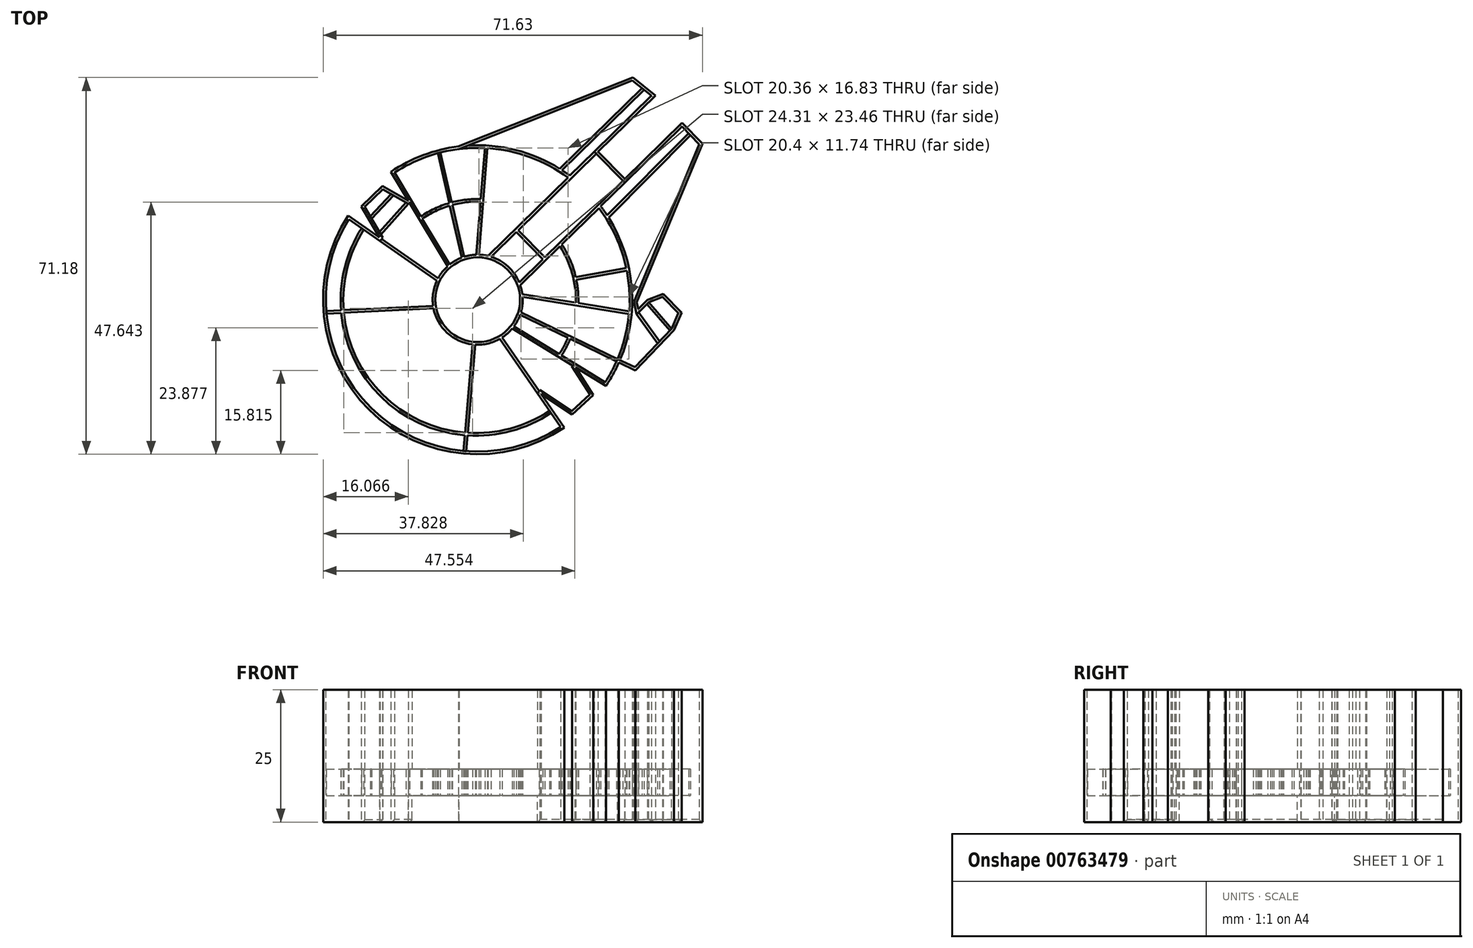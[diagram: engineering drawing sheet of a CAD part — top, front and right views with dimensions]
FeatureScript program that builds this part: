
annotation { "Feature Type Name" : "Feature", "Feature Type Description" : "" }
export const myFeature = defineFeature(function(context is Context, id is Id, definition is map)
    precondition{}
    {
        {
            var Q0;
            Q0=qCreatedBy(makeId("Top.planeOp"),FACE);
            var sketch = newSketch(context, id + "F0", { "sketchPlane" : qUnion([Q0])});
            skArc(sketch, "E0", {"start": v(9.63, 50.7) * mm, "mid": v(13.66, 13.96) * mm, "end": v(50.46, 10.62) * mm});
            skArc(sketch, "E1.0", {"start": v(9.77, 49.99) * mm, "mid": v(6.25, 41.67) * mm, "end": v(5.5, 32.67) * mm});
            skLineSegment(sketch, "E2", {"start": v(9.63, 50.7) * mm, "end": v(15.54, 46.57) * mm});
            skLineSegment(sketch, "E3", {"start": v(15.54, 46.57) * mm, "end": v(12.14, 52.43) * mm});
            skLineSegment(sketch, "E4", {"start": v(12.14, 52.43) * mm, "end": v(16.15, 56.29) * mm});
            skLineSegment(sketch, "E5", {"start": v(16.15, 56.29) * mm, "end": v(21, 53.48) * mm});
            skLineSegment(sketch, "E6", {"start": v(28.43, 41.12) * mm, "end": v(21.26, 53.06) * mm});
            skLineSegment(sketch, "E7.0", {"start": v(16.16, 46.5) * mm, "end": v(15.82, 47.1) * mm});
            skLineSegment(sketch, "E8.0", {"start": v(12.77, 52.34) * mm, "end": v(16.22, 55.67) * mm});
            skLineSegment(sketch, "E9.0", {"start": v(16.22, 55.67) * mm, "end": v(17.8, 54.75) * mm});
            skLineSegment(sketch, "E10.0", {"start": v(28.82, 41.44) * mm, "end": v(23.63, 50.08) * mm});
            skLineSegment(sketch, "E11.trimOffspring", {"start": v(9.77, 49.99) * mm, "end": v(12.18, 48.31) * mm});
            skLineSegment(sketch, "E12", {"start": v(50.46, 10.62) * mm, "end": v(46.07, 16.99) * mm});
            skLineSegment(sketch, "E13", {"start": v(46.07, 16.99) * mm, "end": v(51.9, 13.13) * mm});
            skLineSegment(sketch, "E14", {"start": v(51.9, 13.13) * mm, "end": v(55.96, 16.81) * mm});
            skLineSegment(sketch, "E15", {"start": v(55.96, 16.81) * mm, "end": v(52.61, 22.01) * mm});
            skLineSegment(sketch, "E16", {"start": v(40.62, 29.33) * mm, "end": v(52.03, 22.37) * mm});
            skLineSegment(sketch, "E17.0", {"start": v(40.93, 29.73) * mm, "end": v(49.49, 24.5) * mm});
            skLineSegment(sketch, "E18.0", {"start": v(55.31, 16.9) * mm, "end": v(51.86, 22.26) * mm});
            skLineSegment(sketch, "E19.0", {"start": v(51.86, 13.76) * mm, "end": v(55.31, 16.9) * mm});
            skLineSegment(sketch, "E20.0", {"start": v(45.82, 17.75) * mm, "end": v(51.86, 13.76) * mm});
            skLineSegment(sketch, "E21", {"start": v(45.69, 17.55) * mm, "end": v(45.82, 17.75) * mm});
            skLineSegment(sketch, "E22", {"start": v(51.86, 22.26) * mm, "end": v(52.03, 22.37) * mm});
            skLineSegment(sketch, "E23", {"start": v(16, 46.26) * mm, "end": v(16.16, 46.5) * mm});
            skLineSegment(sketch, "E24", {"start": v(21.26, 53.06) * mm, "end": v(21, 52.9) * mm});
            skLineSegment(sketch, "E25", {"start": v(30.49, 63.76) * mm, "end": v(63.42, 76.78) * mm});
            skLineSegment(sketch, "E26", {"start": v(63.42, 76.78) * mm, "end": v(67.67, 73.38) * mm});
            skLineSegment(sketch, "E27", {"start": v(67.67, 73.38) * mm, "end": v(56.84, 62.75) * mm});
            skLineSegment(sketch, "E28", {"start": v(56.84, 62.75) * mm, "end": v(61.89, 57.61) * mm});
            skLineSegment(sketch, "E29", {"start": v(72.68, 68.22) * mm, "end": v(76.55, 64.28) * mm});
            skLineSegment(sketch, "E30", {"start": v(76.55, 64.28) * mm, "end": v(64.13, 34.33) * mm});
            skLineSegment(sketch, "E31", {"start": v(64.13, 34.33) * mm, "end": v(64.43, 33.03) * mm});
            skLineSegment(sketch, "E32", {"start": v(64.43, 33.03) * mm, "end": v(66.16, 34.73) * mm});
            skLineSegment(sketch, "E33", {"start": v(66.16, 34.73) * mm, "end": v(69.15, 35.9) * mm});
            skLineSegment(sketch, "E34", {"start": v(69.15, 35.9) * mm, "end": v(72.63, 32.36) * mm});
            skLineSegment(sketch, "E35", {"start": v(72.63, 32.36) * mm, "end": v(71.16, 29.04) * mm});
            skLineSegment(sketch, "E36", {"start": v(71.16, 29.04) * mm, "end": v(63.9, 21.43) * mm});
            skLineSegment(sketch, "E37", {"start": v(63.9, 21.43) * mm, "end": v(60.78, 22.93) * mm});
            skLineSegment(sketch, "E38.0", {"start": v(32.27, 63.93) * mm, "end": v(63.33, 76.2) * mm});
            skLineSegment(sketch, "E39.0", {"start": v(63.33, 76.2) * mm, "end": v(65.12, 74.78) * mm});
            skLineSegment(sketch, "E40.0", {"start": v(66.91, 73.34) * mm, "end": v(51.52, 58.22) * mm});
            skLineSegment(sketch, "E41.0", {"start": v(56.49, 62.4) * mm, "end": v(61.53, 57.26) * mm});
            skLineSegment(sketch, "E42.0", {"start": v(42.16, 37.53) * mm, "end": v(49.64, 44.88) * mm});
            skLineSegment(sketch, "E43.0", {"start": v(72.68, 67.51) * mm, "end": v(73.94, 66.22) * mm});
            skLineSegment(sketch, "E44.0", {"start": v(75.96, 64.17) * mm, "end": v(63.61, 34.37) * mm});
            skLineSegment(sketch, "E45.0", {"start": v(63.61, 34.37) * mm, "end": v(64.13, 32.04) * mm});
            skLineSegment(sketch, "E46.0", {"start": v(64.5, 32.4) * mm, "end": v(66.08, 33.95) * mm});
            skLineSegment(sketch, "E47.0", {"start": v(66.44, 34.3) * mm, "end": v(69.03, 35.31) * mm});
            skLineSegment(sketch, "E48.0", {"start": v(69.03, 35.31) * mm, "end": v(72.03, 32.26) * mm});
            skLineSegment(sketch, "E49.0", {"start": v(72.03, 32.26) * mm, "end": v(70.73, 29.32) * mm});
            skLineSegment(sketch, "E50.0", {"start": v(70.39, 28.96) * mm, "end": v(68.44, 26.92) * mm});
            skLineSegment(sketch, "E51.0", {"start": v(63.78, 22.04) * mm, "end": v(60.98, 23.4) * mm});
            skArc(sketch, "E52.trimOffspring", {"start": v(51.52, 58.22) * mm, "mid": v(50.79, 58.75) * mm, "end": v(50.04, 59.26) * mm});
            skArc(sketch, "E53.trimOffspring", {"start": v(51.16, 57.87) * mm, "mid": v(43.96, 61.74) * mm, "end": v(35.97, 63.43) * mm});
            skArc(sketch, "E54.trimOffspring", {"start": v(58.34, 18.52) * mm, "mid": v(59.66, 20.67) * mm, "end": v(60.78, 22.93) * mm});
            skArc(sketch, "E55.trimOffspring", {"start": v(58.2, 19.2) * mm, "mid": v(59.34, 21.13) * mm, "end": v(60.33, 23.15) * mm});
            skLineSegment(sketch, "E56.trimOffspring", {"start": v(56.49, 62.4) * mm, "end": v(41.75, 47.92) * mm});
            skLineSegment(sketch, "E57.trimOffspring", {"start": v(61.89, 57.61) * mm, "end": v(72.68, 68.22) * mm});
            skLineSegment(sketch, "E58", {"start": v(73.94, 66.22) * mm, "end": v(58.57, 50.73) * mm});
            skLineSegment(sketch, "E59.0", {"start": v(74.3, 65.87) * mm, "end": v(58.84, 50.3) * mm});
            skLineSegment(sketch, "E60", {"start": v(62.27, 40.3) * mm, "end": v(52.74, 38.57) * mm});
            skLineSegment(sketch, "E61.0", {"start": v(62.17, 40.78) * mm, "end": v(52.64, 39.06) * mm});
            skLineSegment(sketch, "E62.trimOffspring", {"start": v(49.76, 10.75) * mm, "end": v(47.95, 13.39) * mm});
            skArc(sketch, "E63.trimOffspring", {"start": v(60.98, 23.4) * mm, "mid": v(63.2, 37.1) * mm, "end": v(58.84, 50.3) * mm});
            skArc(sketch, "E64.trimOffspring", {"start": v(62.17, 40.78) * mm, "mid": v(60.2, 46.73) * mm, "end": v(57, 52.11) * mm});
            skArc(sketch, "E65.trimOffspring", {"start": v(58.57, 50.73) * mm, "mid": v(57.97, 51.6) * mm, "end": v(57.35, 52.46) * mm});
            skLineSegment(sketch, "E66.trimOffspring", {"start": v(57.35, 52.46) * mm, "end": v(72.68, 67.51) * mm});
            skLineSegment(sketch, "E67.trimOffspring", {"start": v(51.16, 57.87) * mm, "end": v(36.09, 43.06) * mm});
            skLineSegment(sketch, "E68", {"start": v(50.04, 59.26) * mm, "end": v(65.51, 74.46) * mm});
            skLineSegment(sketch, "E69.0", {"start": v(49.6, 59.53) * mm, "end": v(65.12, 74.78) * mm});
            skLineSegment(sketch, "E70.trimOffspring", {"start": v(65.51, 74.46) * mm, "end": v(66.91, 73.34) * mm});
            skArc(sketch, "E71.trimOffspring", {"start": v(30.49, 63.76) * mm, "mid": v(23.82, 62.11) * mm, "end": v(17.72, 58.95) * mm});
            skLineSegment(sketch, "E72", {"start": v(35.97, 63.43) * mm, "end": v(34.33, 43.3) * mm});
            skArc(sketch, "E73", {"start": v(41.96, 38.05) * mm, "mid": v(39.84, 41.07) * mm, "end": v(36.65, 42.9) * mm});
            skCircle(sketch, "E74.0", {"center": v(34.1, 34.8) * mm, "radius": 8 * mm});
            skLineSegment(sketch, "E75.trimOffspring", {"start": v(41.96, 38.05) * mm, "end": v(46.44, 42.44) * mm});
            skArc(sketch, "E76.trimOffspring", {"start": v(36.09, 43.06) * mm, "mid": v(35.22, 43.22) * mm, "end": v(34.33, 43.3) * mm});
            skLineSegment(sketch, "E77", {"start": v(27.06, 62.6) * mm, "end": v(29.21, 53.19) * mm});
            skLineSegment(sketch, "E78", {"start": v(62.67, 32.1) * mm, "end": v(42.6, 35.35) * mm});
            skArc(sketch, "E79.trimOffspring", {"start": v(42.27, 32.43) * mm, "mid": v(42.56, 33.87) * mm, "end": v(42.6, 35.35) * mm});
            skLineSegment(sketch, "E80.trimOffspring", {"start": v(60.53, 23.6) * mm, "end": v(42.27, 32.43) * mm});
            skArc(sketch, "E81.trimOffspring", {"start": v(60.53, 23.6) * mm, "mid": v(61.93, 27.77) * mm, "end": v(62.67, 32.1) * mm});
            skLineSegment(sketch, "E82.trimOffspring", {"start": v(60.33, 23.15) * mm, "end": v(51.6, 27.37) * mm});
            skArc(sketch, "E83.trimOffspring", {"start": v(38.72, 27.66) * mm, "mid": v(39.74, 28.42) * mm, "end": v(40.62, 29.33) * mm});
            skLineSegment(sketch, "E84.trimOffspring", {"start": v(45.69, 17.55) * mm, "end": v(38.72, 27.66) * mm});
            skLineSegment(sketch, "E85.trimOffspring", {"start": v(52.61, 22.01) * mm, "end": v(58.34, 18.52) * mm});
            skArc(sketch, "E86.trimOffspring", {"start": v(40.93, 29.73) * mm, "mid": v(41.6, 30.8) * mm, "end": v(42.12, 31.95) * mm});
            skLineSegment(sketch, "E87", {"start": v(31.93, 6.19) * mm, "end": v(32.18, 9.15) * mm});
            skLineSegment(sketch, "E88", {"start": v(5.5, 32.67) * mm, "end": v(8.3, 32.8) * mm});
            skLineSegment(sketch, "E89.0", {"start": v(5.54, 32.17) * mm, "end": v(8.33, 32.3) * mm});
            skLineSegment(sketch, "E90.0", {"start": v(31.43, 6.23) * mm, "end": v(31.68, 9.19) * mm});
            skArc(sketch, "E91.trimOffspring", {"start": v(31.93, 6.19) * mm, "mid": v(41.22, 7) * mm, "end": v(49.76, 10.75) * mm});
            skArc(sketch, "E92.trimOffspring", {"start": v(5.54, 32.17) * mm, "mid": v(13.8, 14.53) * mm, "end": v(31.43, 6.23) * mm});
            skArc(sketch, "E93.trimOffspring", {"start": v(25.77, 33.14) * mm, "mid": v(28.35, 28.54) * mm, "end": v(33.14, 26.35) * mm});
            skLineSegment(sketch, "E94.trimOffspring", {"start": v(16, 46.26) * mm, "end": v(26.63, 38.84) * mm});
            skArc(sketch, "E95.trimOffspring", {"start": v(26.4, 38.39) * mm, "mid": v(25.7, 36.07) * mm, "end": v(25.69, 33.64) * mm});
            skArc(sketch, "E96.trimOffspring", {"start": v(33.64, 26.3) * mm, "mid": v(36.05, 26.52) * mm, "end": v(38.3, 27.4) * mm});
            skArc(sketch, "E97.trimOffspring", {"start": v(28.43, 41.12) * mm, "mid": v(27.43, 40.06) * mm, "end": v(26.63, 38.84) * mm});
            skLineSegment(sketch, "E98", {"start": v(46.8, 42.8) * mm, "end": v(41.75, 47.92) * mm});
            skLineSegment(sketch, "E99.0", {"start": v(46.44, 42.44) * mm, "end": v(41.4, 47.57) * mm});
            skLineSegment(sketch, "E100.trimOffspring", {"start": v(46.8, 42.8) * mm, "end": v(61.53, 57.26) * mm});
            skLineSegment(sketch, "E101.trimOffspring", {"start": v(41.4, 47.57) * mm, "end": v(36.64, 42.9) * mm});
            skArc(sketch, "E102.trimOffspring", {"start": v(49.91, 24.25) * mm, "mid": v(50.83, 25.77) * mm, "end": v(51.6, 27.37) * mm});
            skArc(sketch, "E103.trimOffspring", {"start": v(53.1, 34.15) * mm, "mid": v(53.06, 36.37) * mm, "end": v(52.74, 38.57) * mm});
            skArc(sketch, "E104.trimOffspring", {"start": v(34.69, 53.82) * mm, "mid": v(31.93, 53.7) * mm, "end": v(29.21, 53.19) * mm});
            skLineSegment(sketch, "E105.0", {"start": v(62.72, 32.6) * mm, "end": v(53.1, 34.15) * mm});
            skArc(sketch, "E106.0", {"start": v(52.61, 34.23) * mm, "mid": v(51.94, 39.79) * mm, "end": v(49.64, 44.88) * mm});
            skLineSegment(sketch, "E107.0", {"start": v(26.58, 62.48) * mm, "end": v(28.73, 53.05) * mm});
            skLineSegment(sketch, "E108.0", {"start": v(35.47, 63.45) * mm, "end": v(34.69, 53.82) * mm});
            skArc(sketch, "E109.0", {"start": v(49.49, 24.5) * mm, "mid": v(50.4, 26) * mm, "end": v(51.15, 27.59) * mm});
            skLineSegment(sketch, "E110.trimOffspring", {"start": v(49.91, 24.25) * mm, "end": v(58.2, 19.2) * mm});
            skLineSegment(sketch, "E111.trimOffspring", {"start": v(51.15, 27.59) * mm, "end": v(42.12, 31.95) * mm});
            skLineSegment(sketch, "E112.trimOffspring", {"start": v(52.61, 34.23) * mm, "end": v(42.54, 35.86) * mm});
            skArc(sketch, "E113.trimOffspring", {"start": v(52.64, 39.06) * mm, "mid": v(51.6, 42.27) * mm, "end": v(50, 45.24) * mm});
            skLineSegment(sketch, "E114.trimOffspring", {"start": v(50, 45.24) * mm, "end": v(57, 52.11) * mm});
            skArc(sketch, "E115.trimOffspring", {"start": v(33.83, 43.29) * mm, "mid": v(32.68, 43.17) * mm, "end": v(31.56, 42.9) * mm});
            skArc(sketch, "E116.trimOffspring", {"start": v(31.08, 42.74) * mm, "mid": v(29.9, 42.18) * mm, "end": v(28.82, 41.44) * mm});
            skArc(sketch, "E117.trimOffspring", {"start": v(28.84, 52.56) * mm, "mid": v(26.14, 51.52) * mm, "end": v(23.63, 50.08) * mm});
            skLineSegment(sketch, "E118.trimOffspring", {"start": v(29.32, 52.7) * mm, "end": v(31.56, 42.9) * mm});
            skArc(sketch, "E119.trimOffspring", {"start": v(28.73, 53.05) * mm, "mid": v(25.95, 51.99) * mm, "end": v(23.37, 50.5) * mm});
            skLineSegment(sketch, "E120.trimOffspring", {"start": v(28.84, 52.56) * mm, "end": v(31.08, 42.74) * mm});
            skLineSegment(sketch, "E121.trimOffspring", {"start": v(34.65, 53.32) * mm, "end": v(33.83, 43.29) * mm});
            skArc(sketch, "E122.trimOffspring", {"start": v(34.65, 53.32) * mm, "mid": v(31.96, 53.2) * mm, "end": v(29.32, 52.7) * mm});
            skArc(sketch, "E123.trimOffspring", {"start": v(42.54, 35.86) * mm, "mid": v(42.4, 36.7) * mm, "end": v(42.16, 37.53) * mm});
            skArc(sketch, "E124.trimOffspring", {"start": v(35.47, 63.45) * mm, "mid": v(31.23, 63.34) * mm, "end": v(27.06, 62.6) * mm});
            skArc(sketch, "E125.trimOffspring", {"start": v(26.58, 62.48) * mm, "mid": v(22.34, 60.96) * mm, "end": v(18.4, 58.8) * mm});
            skArc(sketch, "E126", {"start": v(12.59, 48.02) * mm, "mid": v(9.47, 40.73) * mm, "end": v(8.79, 32.83) * mm});
            skPoint(sketch, "E126.endSnap0", {"position": v(48.27, 13.8) * mm});
            skArc(sketch, "E127.0", {"start": v(12.18, 48.31) * mm, "mid": v(8.99, 40.87) * mm, "end": v(8.3, 32.8) * mm});
            skArc(sketch, "E128.trimOffspring", {"start": v(32.22, 9.65) * mm, "mid": v(40.28, 10.46) * mm, "end": v(47.66, 13.8) * mm});
            skLineSegment(sketch, "E129.trimOffspring", {"start": v(32.22, 9.65) * mm, "end": v(33.64, 26.3) * mm});
            skArc(sketch, "E130.trimOffspring", {"start": v(32.18, 9.15) * mm, "mid": v(40.41, 9.98) * mm, "end": v(47.95, 13.39) * mm});
            skLineSegment(sketch, "E131.trimOffspring", {"start": v(31.73, 9.69) * mm, "end": v(33.14, 26.35) * mm});
            skLineSegment(sketch, "E132.trimOffspring", {"start": v(8.79, 32.83) * mm, "end": v(25.69, 33.64) * mm});
            skLineSegment(sketch, "E133.trimOffspring", {"start": v(8.83, 32.33) * mm, "end": v(25.77, 33.14) * mm});
            skArc(sketch, "E134.trimOffspring", {"start": v(8.33, 32.3) * mm, "mid": v(15.8, 16.5) * mm, "end": v(31.68, 9.19) * mm});
            skArc(sketch, "E135.trimOffspring", {"start": v(8.83, 32.33) * mm, "mid": v(16.16, 16.84) * mm, "end": v(31.73, 9.69) * mm});
            skLineSegment(sketch, "E136.trimOffspring", {"start": v(12.59, 48.02) * mm, "end": v(26.4, 38.39) * mm});
            skLineSegment(sketch, "E137.trimOffspring", {"start": v(21, 53.48) * mm, "end": v(17.72, 58.95) * mm});
            skLineSegment(sketch, "E138", {"start": v(66.44, 34.3) * mm, "end": v(70.73, 29.32) * mm});
            skLineSegment(sketch, "E139", {"start": v(64.13, 32.04) * mm, "end": v(68.09, 26.55) * mm});
            skLineSegment(sketch, "E140.0", {"start": v(64.5, 32.4) * mm, "end": v(68.44, 26.92) * mm});
            skLineSegment(sketch, "E141.0", {"start": v(66.08, 33.95) * mm, "end": v(70.39, 28.96) * mm});
            skLineSegment(sketch, "E142.trimOffspring", {"start": v(68.09, 26.55) * mm, "end": v(63.78, 22.04) * mm});
            skLineSegment(sketch, "E143", {"start": v(15.82, 47.1) * mm, "end": v(21, 52.9) * mm});
            skLineSegment(sketch, "E144", {"start": v(14.07, 50.1) * mm, "end": v(18.25, 54.5) * mm});
            skLineSegment(sketch, "E145.0", {"start": v(13.8, 50.56) * mm, "end": v(17.8, 54.75) * mm});
            skLineSegment(sketch, "E146.0", {"start": v(15.55, 47.55) * mm, "end": v(20.56, 53.16) * mm});
            skLineSegment(sketch, "E147.trimOffspring", {"start": v(15.55, 47.55) * mm, "end": v(14.07, 50.1) * mm});
            skLineSegment(sketch, "E148.trimOffspring", {"start": v(13.8, 50.56) * mm, "end": v(12.77, 52.34) * mm});
            skLineSegment(sketch, "E149.trimOffspring", {"start": v(18.25, 54.5) * mm, "end": v(20.56, 53.16) * mm});
            skLineSegment(sketch, "E150.trimOffspring", {"start": v(47.66, 13.8) * mm, "end": v(38.3, 27.4) * mm});
            skLineSegment(sketch, "E151.trimOffspring", {"start": v(74.3, 65.87) * mm, "end": v(75.96, 64.17) * mm});
            skArc(sketch, "E152.trimOffspring", {"start": v(49.6, 59.53) * mm, "mid": v(41.28, 63.1) * mm, "end": v(32.27, 63.93) * mm});
            skArc(sketch, "E153.trimOffspring", {"start": v(62.72, 32.6) * mm, "mid": v(62.75, 36.46) * mm, "end": v(62.27, 40.3) * mm});
            skLineSegment(sketch, "E154.trimOffspring", {"start": v(23.37, 50.5) * mm, "end": v(18.4, 58.8) * mm});
            skSolve(sketch);
        }
        {
            var Q0;
            Q0=makeQuery(id+"F0.imprint","IMPRINT",FACE,{"disambiguationData":[TD([[makeQuery(id+"F0.imprint","IMPRINT",EDGE,{"derivedFrom":sQuery(id+"F0.wireOp",EDGE,"3ed46772-27a6-4d94-b4a7-c1b057d9c120.2.1")}),1.0]])]});
            var Q1;
            Q1=makeQuery(id+"F0.imprint","IMPRINT",FACE,{"disambiguationData":[TD([[makeQuery(id+"F0.imprint","IMPRINT",EDGE,{"derivedFrom":sQuery(id+"F0.wireOp",EDGE,"3ed46772-27a6-4d94-b4a7-c1b057d9c120.1.1")}),1.0]])]});
            var Q2;
            Q2=makeQuery(id+"F0.imprint","IMPRINT",FACE,{"disambiguationData":[TD([[makeQuery(id+"F0.imprint","IMPRINT",EDGE,{"derivedFrom":sQuery(id+"F0.wireOp",EDGE,"3iVvSaAU-kiet-Srhm-uzs1-kmzdiTIg7kjV")}),-1.0]])]});
            var Q3;
            Q3=makeQuery(id+"F0.imprint","IMPRINT",FACE,{"disambiguationData":[TD([[makeQuery(id+"F0.imprint","IMPRINT",EDGE,{"derivedFrom":sQuery(id+"F0.wireOp",EDGE,"gFyHxgtJ-ju8G-WbUf-OddL-X56tFMkTOzbv")}),1.0]])]});
            var Q4;
            Q4=makeQuery(id+"F0.imprint","IMPRINT",FACE,{"disambiguationData":[TD([[makeQuery(id+"F0.imprint","IMPRINT",EDGE,{"derivedFrom":sQuery(id+"F0.wireOp",EDGE,"a3401636-6155-42f7-9479-38b70ebc3d2b.1.0")}),1.0]])]});
            var Q5;
            Q5=makeQuery(id+"F0.imprint","IMPRINT",FACE,{"disambiguationData":[TD([[makeQuery(id+"F0.imprint","IMPRINT",EDGE,{"derivedFrom":sQuery(id+"F0.wireOp",EDGE,"a3401636-6155-42f7-9479-38b70ebc3d2b.2.0")}),1.0]])]});
            var Q6;
            Q6=makeQuery(id+"F0.imprint","IMPRINT",FACE,{"disambiguationData":[TD([[makeQuery(id+"F0.imprint","IMPRINT",EDGE,{"derivedFrom":sQuery(id+"F0.wireOp",EDGE,"e8Qt5wkm-OQUc-Hg0l-7nr0-fbRjWDWY3zNd")}),-1.0]])]});
            var Q7;
            Q7=makeQuery(id+"F0.imprint","IMPRINT",FACE,{"disambiguationData":[TD([[makeQuery(id+"F0.imprint","IMPRINT",EDGE,{"derivedFrom":sQuery(id+"F0.wireOp",EDGE,"2Ig4vxbF-eVPD-97Q4-TkuO-rgopO8nLGlP4")}),-1.0]])]});
            var Q8;
            Q8=makeQuery(id+"F0.imprint","IMPRINT",FACE,{"disambiguationData":[TD([[makeQuery(id+"F0.imprint","IMPRINT",EDGE,{"derivedFrom":sQuery(id+"F0.wireOp",EDGE,"u05zh7sX-OJC8-3TQU-wVel-wsQ1eLN49gEu")}),1.0]])]});
            var Q9;
            Q9=makeQuery(id+"F0.imprint","IMPRINT",FACE,{"disambiguationData":[TD([[makeQuery(id+"F0.imprint","IMPRINT",EDGE,{"derivedFrom":sQuery(id+"F0.wireOp",EDGE,"xzO9axfg-FktW-NyAH-tsz7-sGytwWePR5oS")}),1.0]])]});
            var Q10;
            Q10=makeQuery(id+"F0.imprint","IMPRINT",FACE,{"disambiguationData":[TD([[makeQuery(id+"F0.imprint","IMPRINT",EDGE,{"derivedFrom":sQuery(id+"F0.wireOp",EDGE,"E0")}),1.0]])]});
            extrude(context, id + "F1", {"entities" : qUnion([Q0, Q1, Q2, Q3, Q4, Q5, Q6, Q7, Q8, Q9, Q10]), "depth" : 25 * mm, "offsetDistance" : 25 * mm});
        }
        {
            var Q0;
            Q0=qCreatedBy(makeId("Top.planeOp"),FACE);
            cPlane(context, id + "F2", {"entities" : qUnion([Q0]), "cplaneType" : CPlaneType.OFFSET, "offset" : 5 * mm, "width" : 150 * mm, "height" : 150 * mm});
        }
        {
            var Q0;
            Q0=qCreatedBy(id+"F2.planeOp",FACE);
            var sketch = newSketch(context, id + "F3", { "sketchPlane" : qUnion([Q0])});
            skArc(sketch, "E155.0", {"start": v(9.77, 49.99) * mm, "mid": v(6.25, 41.67) * mm, "end": v(5.5, 32.67) * mm});
            skLineSegment(sketch, "E156.0", {"start": v(16.16, 46.5) * mm, "end": v(15.55, 47.55) * mm});
            skLineSegment(sketch, "E157.0", {"start": v(12.77, 52.34) * mm, "end": v(16.22, 55.67) * mm});
            skLineSegment(sketch, "E158.0", {"start": v(16.22, 55.67) * mm, "end": v(18.25, 54.5) * mm});
            skLineSegment(sketch, "E159.trimOffspring", {"start": v(9.77, 49.99) * mm, "end": v(15.7, 45.85) * mm});
            skLineSegment(sketch, "E160.0", {"start": v(55.31, 16.9) * mm, "end": v(51.86, 22.26) * mm});
            skLineSegment(sketch, "E161.0", {"start": v(51.86, 13.76) * mm, "end": v(55.31, 16.9) * mm});
            skLineSegment(sketch, "E162.0", {"start": v(45.82, 17.75) * mm, "end": v(51.86, 13.76) * mm});
            skLineSegment(sketch, "E163", {"start": v(45.39, 17.1) * mm, "end": v(45.82, 17.75) * mm});
            skLineSegment(sketch, "E164", {"start": v(51.86, 22.26) * mm, "end": v(52.5, 22.67) * mm});
            skLineSegment(sketch, "E165", {"start": v(15.7, 45.85) * mm, "end": v(16.16, 46.5) * mm});
            skLineSegment(sketch, "E166", {"start": v(21.69, 53.31) * mm, "end": v(21, 52.9) * mm});
            skLineSegment(sketch, "E167.0", {"start": v(30.61, 63.27) * mm, "end": v(63.33, 76.2) * mm});
            skLineSegment(sketch, "E168.0", {"start": v(63.33, 76.2) * mm, "end": v(66.91, 73.34) * mm});
            skLineSegment(sketch, "E169.0", {"start": v(66.91, 73.34) * mm, "end": v(56.14, 62.75) * mm});
            skLineSegment(sketch, "E170.0", {"start": v(56.14, 62.75) * mm, "end": v(61.88, 56.9) * mm});
            skLineSegment(sketch, "E171.0", {"start": v(72.68, 67.51) * mm, "end": v(75.96, 64.17) * mm});
            skLineSegment(sketch, "E172.0", {"start": v(75.96, 64.17) * mm, "end": v(63.61, 34.37) * mm});
            skLineSegment(sketch, "E173.0", {"start": v(63.61, 34.37) * mm, "end": v(64.13, 32.04) * mm});
            skLineSegment(sketch, "E174.0", {"start": v(64.13, 32.04) * mm, "end": v(66.44, 34.3) * mm});
            skLineSegment(sketch, "E175.0", {"start": v(66.44, 34.3) * mm, "end": v(69.03, 35.31) * mm});
            skLineSegment(sketch, "E176.0", {"start": v(69.03, 35.31) * mm, "end": v(72.03, 32.26) * mm});
            skLineSegment(sketch, "E177.0", {"start": v(72.03, 32.26) * mm, "end": v(70.73, 29.32) * mm});
            skLineSegment(sketch, "E178.0", {"start": v(70.73, 29.32) * mm, "end": v(68.09, 26.55) * mm});
            skLineSegment(sketch, "E179.0", {"start": v(63.78, 22.04) * mm, "end": v(60.53, 23.6) * mm});
            skArc(sketch, "E180.trimOffspring", {"start": v(58.2, 19.2) * mm, "mid": v(59.46, 21.35) * mm, "end": v(60.53, 23.6) * mm});
            skLineSegment(sketch, "E181.0", {"start": v(74.3, 65.87) * mm, "end": v(74.3, 65.87) * mm});
            skLineSegment(sketch, "E182.trimOffspring", {"start": v(49.76, 10.75) * mm, "end": v(47.95, 13.39) * mm});
            skLineSegment(sketch, "E183.trimOffspring", {"start": v(61.88, 56.9) * mm, "end": v(72.68, 67.51) * mm});
            skArc(sketch, "E184.trimOffspring", {"start": v(31.43, 6.23) * mm, "mid": v(40.98, 6.94) * mm, "end": v(49.76, 10.75) * mm});
            skArc(sketch, "E185.trimOffspring", {"start": v(5.5, 32.67) * mm, "mid": v(13.63, 14.7) * mm, "end": v(31.43, 6.23) * mm});
            skLineSegment(sketch, "E186.trimOffspring", {"start": v(52.5, 22.67) * mm, "end": v(58.2, 19.2) * mm});
            skArc(sketch, "E187.trimOffspring", {"start": v(30.61, 63.27) * mm, "mid": v(28.83, 63) * mm, "end": v(27.06, 62.6) * mm});
            skArc(sketch, "E188.trimOffspring", {"start": v(27.06, 62.6) * mm, "mid": v(22.57, 61.06) * mm, "end": v(18.4, 58.8) * mm});
            skPoint(sketch, "E189.endSnap0", {"position": v(48.27, 13.8) * mm});
            skLineSegment(sketch, "E190.trimOffspring", {"start": v(68.09, 26.55) * mm, "end": v(63.78, 22.04) * mm});
            skLineSegment(sketch, "E191.trimOffspring", {"start": v(15.55, 47.55) * mm, "end": v(13.8, 50.56) * mm});
            skLineSegment(sketch, "E192.trimOffspring", {"start": v(13.8, 50.56) * mm, "end": v(12.77, 52.34) * mm});
            skLineSegment(sketch, "E193.trimOffspring", {"start": v(18.25, 54.5) * mm, "end": v(21, 52.9) * mm});
            skLineSegment(sketch, "E194.trimOffspring", {"start": v(47.95, 13.39) * mm, "end": v(45.39, 17.1) * mm});
            skLineSegment(sketch, "E195.trimOffspring", {"start": v(21.69, 53.31) * mm, "end": v(18.4, 58.8) * mm});
            skPoint(sketch, "E196.trimOffspring.end.orphan", {"position": v(47.66, 13.8) * mm});
            skSolve(sketch);
        }
        {
            var Q0;
            Q0 = qSketchRegion(id + "F3", true);
            extrude(context, id + "F4", {"entities" : qUnion([Q0]), "operationType" : NewBodyOperationType.REMOVE, "oppositeDirection" : true, "depth" : 5 * mm, "offsetDistance" : 25 * mm});
        }
        {
            var Q0;
            Q0=qCreatedBy(id+"F2.planeOp",FACE);
            cPlane(context, id + "F5", {"entities" : qUnion([Q0]), "cplaneType" : CPlaneType.OFFSET, "offset" : 5 * mm, "width" : 150 * mm, "height" : 150 * mm});
        }
        {
            var Q0;
            Q0=qCreatedBy(id+"F5.planeOp",FACE);
            var sketch = newSketch(context, id + "F6", { "sketchPlane" : qUnion([Q0])});
            skArc(sketch, "E197.0", {"start": v(9.77, 49.99) * mm, "mid": v(6.25, 41.67) * mm, "end": v(5.5, 32.67) * mm});
            skLineSegment(sketch, "E198.0", {"start": v(16.16, 46.5) * mm, "end": v(15.55, 47.55) * mm});
            skLineSegment(sketch, "E199.0", {"start": v(12.77, 52.34) * mm, "end": v(16.22, 55.67) * mm});
            skLineSegment(sketch, "E200.0", {"start": v(16.22, 55.67) * mm, "end": v(18.25, 54.5) * mm});
            skLineSegment(sketch, "E201.trimOffspring", {"start": v(9.77, 49.99) * mm, "end": v(15.7, 45.85) * mm});
            skLineSegment(sketch, "E202.0", {"start": v(55.31, 16.9) * mm, "end": v(51.86, 22.26) * mm});
            skLineSegment(sketch, "E203.0", {"start": v(51.86, 13.76) * mm, "end": v(55.31, 16.9) * mm});
            skLineSegment(sketch, "E204.0", {"start": v(45.82, 17.75) * mm, "end": v(51.86, 13.76) * mm});
            skLineSegment(sketch, "E205", {"start": v(45.39, 17.1) * mm, "end": v(45.82, 17.75) * mm});
            skLineSegment(sketch, "E206", {"start": v(51.86, 22.26) * mm, "end": v(52.5, 22.67) * mm});
            skLineSegment(sketch, "E207", {"start": v(15.7, 45.85) * mm, "end": v(16.16, 46.5) * mm});
            skLineSegment(sketch, "E208", {"start": v(21.69, 53.31) * mm, "end": v(21, 52.9) * mm});
            skLineSegment(sketch, "E209.0", {"start": v(30.61, 63.27) * mm, "end": v(63.33, 76.2) * mm});
            skLineSegment(sketch, "E210.0", {"start": v(63.33, 76.2) * mm, "end": v(66.91, 73.34) * mm});
            skLineSegment(sketch, "E211.0", {"start": v(66.91, 73.34) * mm, "end": v(56.14, 62.75) * mm});
            skLineSegment(sketch, "E212.0", {"start": v(56.14, 62.75) * mm, "end": v(61.88, 56.9) * mm});
            skLineSegment(sketch, "E213.0", {"start": v(72.68, 67.51) * mm, "end": v(75.96, 64.17) * mm});
            skLineSegment(sketch, "E214.0", {"start": v(75.96, 64.17) * mm, "end": v(63.61, 34.37) * mm});
            skLineSegment(sketch, "E215.0", {"start": v(63.61, 34.37) * mm, "end": v(64.13, 32.04) * mm});
            skLineSegment(sketch, "E216.0", {"start": v(64.13, 32.04) * mm, "end": v(66.44, 34.3) * mm});
            skLineSegment(sketch, "E217.0", {"start": v(66.44, 34.3) * mm, "end": v(69.03, 35.31) * mm});
            skLineSegment(sketch, "E218.0", {"start": v(69.03, 35.31) * mm, "end": v(72.03, 32.26) * mm});
            skLineSegment(sketch, "E219.0", {"start": v(72.03, 32.26) * mm, "end": v(70.73, 29.32) * mm});
            skLineSegment(sketch, "E220.0", {"start": v(70.73, 29.32) * mm, "end": v(68.09, 26.55) * mm});
            skLineSegment(sketch, "E221.0", {"start": v(63.78, 22.04) * mm, "end": v(60.53, 23.6) * mm});
            skArc(sketch, "E222.trimOffspring", {"start": v(58.2, 19.2) * mm, "mid": v(59.46, 21.35) * mm, "end": v(60.53, 23.6) * mm});
            skLineSegment(sketch, "E223.0", {"start": v(74.3, 65.87) * mm, "end": v(74.3, 65.87) * mm});
            skLineSegment(sketch, "E224.trimOffspring", {"start": v(49.76, 10.75) * mm, "end": v(47.95, 13.39) * mm});
            skLineSegment(sketch, "E225.trimOffspring", {"start": v(61.88, 56.9) * mm, "end": v(72.68, 67.51) * mm});
            skArc(sketch, "E226.trimOffspring", {"start": v(31.43, 6.23) * mm, "mid": v(40.98, 6.94) * mm, "end": v(49.76, 10.75) * mm});
            skArc(sketch, "E227.trimOffspring", {"start": v(5.5, 32.67) * mm, "mid": v(13.63, 14.7) * mm, "end": v(31.43, 6.23) * mm});
            skLineSegment(sketch, "E228.trimOffspring", {"start": v(52.5, 22.67) * mm, "end": v(58.2, 19.2) * mm});
            skArc(sketch, "E229.trimOffspring", {"start": v(30.61, 63.27) * mm, "mid": v(28.83, 63) * mm, "end": v(27.06, 62.6) * mm});
            skArc(sketch, "E230.trimOffspring", {"start": v(27.06, 62.6) * mm, "mid": v(22.57, 61.06) * mm, "end": v(18.4, 58.8) * mm});
            skPoint(sketch, "E231.endSnap0", {"position": v(48.27, 13.8) * mm});
            skLineSegment(sketch, "E232.trimOffspring", {"start": v(68.09, 26.55) * mm, "end": v(63.78, 22.04) * mm});
            skLineSegment(sketch, "E233.trimOffspring", {"start": v(15.55, 47.55) * mm, "end": v(13.8, 50.56) * mm});
            skLineSegment(sketch, "E234.trimOffspring", {"start": v(13.8, 50.56) * mm, "end": v(12.77, 52.34) * mm});
            skLineSegment(sketch, "E235.trimOffspring", {"start": v(18.25, 54.5) * mm, "end": v(21, 52.9) * mm});
            skLineSegment(sketch, "E236.trimOffspring", {"start": v(47.95, 13.39) * mm, "end": v(45.39, 17.1) * mm});
            skLineSegment(sketch, "E237.trimOffspring", {"start": v(21.69, 53.31) * mm, "end": v(18.4, 58.8) * mm});
            skPoint(sketch, "E238.trimOffspring.end.orphan", {"position": v(47.66, 13.8) * mm});
            skSolve(sketch);
        }
        {
            var Q0;
            Q0 = qSketchRegion(id + "F6", true);
            extrude(context, id + "F7", {"entities" : qUnion([Q0]), "operationType" : NewBodyOperationType.REMOVE, "depth" : 15 * mm, "offsetDistance" : 25 * mm});
        }
        {
            var Q0;
            Q0=makeQuery(id+"F1.opExtrude","CAP_EDGE",EDGE,{"disambiguationData":[OSD([sQuery(id+"F0.wireOp",EDGE,"E44.0")])],"isStart":true});
            var Q1;
            Q1=makeQuery(id+"F4.boolean.opBoolean","MERGE",EDGE,{"derivedFrom":[makeQuery(id+"F1.opExtrude","CAP_EDGE",EDGE,{"disambiguationData":[OSD([sQuery(id+"F0.wireOp",EDGE,"E43.0")])],"isStart":true}),makeQuery(id+"F1.opExtrude","CAP_EDGE",EDGE,{"disambiguationData":[OSD([sQuery(id+"F0.wireOp",EDGE,"E151.trimOffspring")])],"isStart":true}),makeQuery(id+"F4.opExtrude","CAP_EDGE",EDGE,{"disambiguationData":[OSD([sQuery(id+"F3.wireOp",EDGE,"E171.0")])],"isStart":false})]});
            var Q2;
            Q2=makeQuery(id+"F1.opExtrude","CAP_EDGE",EDGE,{"disambiguationData":[OSD([sQuery(id+"F0.wireOp",EDGE,"E66.trimOffspring")])],"isStart":true});
            var Q3;
            Q3=makeQuery(id+"F4.boolean.opBoolean","MERGE",EDGE,{"derivedFrom":[makeQuery(id+"F1.opExtrude","CAP_EDGE",EDGE,{"disambiguationData":[OSD([sQuery(id+"F0.wireOp",EDGE,"E41.0")])],"isStart":true}),makeQuery(id+"F4.opExtrude","CAP_EDGE",EDGE,{"disambiguationData":[OSD([sQuery(id+"F3.wireOp",EDGE,"E170.0")])],"isStart":false})]});
            var Q4;
            Q4=makeQuery(id+"F1.opExtrude","CAP_EDGE",EDGE,{"disambiguationData":[OSD([sQuery(id+"F0.wireOp",EDGE,"E40.0")])],"isStart":true});
            var Q5;
            Q5=makeQuery(id+"F4.boolean.opBoolean","MERGE",EDGE,{"derivedFrom":[makeQuery(id+"F1.opExtrude","CAP_EDGE",EDGE,{"disambiguationData":[OSD([sQuery(id+"F0.wireOp",EDGE,"E39.0")])],"isStart":true}),makeQuery(id+"F1.opExtrude","CAP_EDGE",EDGE,{"disambiguationData":[OSD([sQuery(id+"F0.wireOp",EDGE,"E70.trimOffspring")])],"isStart":true}),makeQuery(id+"F4.opExtrude","CAP_EDGE",EDGE,{"disambiguationData":[OSD([sQuery(id+"F3.wireOp",EDGE,"E168.0")])],"isStart":false})]});
            var Q6;
            Q6=makeQuery(id+"F4.boolean.opBoolean","MERGE",EDGE,{"derivedFrom":[makeQuery(id+"F1.opExtrude","CAP_EDGE",EDGE,{"disambiguationData":[OSD([sQuery(id+"F0.wireOp",EDGE,"E38.0")])],"isStart":true}),makeQuery(id+"F4.opExtrude","CAP_EDGE",EDGE,{"disambiguationData":[OSD([sQuery(id+"F3.wireOp",EDGE,"E167.0")])],"isStart":false})]});
            var Q7;
            Q7=makeQuery(id+"F4.boolean.opBoolean","MERGE",EDGE,{"derivedFrom":[makeQuery(id+"F1.opExtrude","CAP_EDGE",EDGE,{"disambiguationData":[OSD([sQuery(id+"F0.wireOp",EDGE,"E124.trimOffspring")])],"isStart":true}),makeQuery(id+"F1.opExtrude","CAP_EDGE",EDGE,{"disambiguationData":[OSD([sQuery(id+"F0.wireOp",EDGE,"E125.trimOffspring")])],"isStart":true}),makeQuery(id+"F4.opExtrude","CAP_EDGE",EDGE,{"disambiguationData":[OSD([sQuery(id+"F3.wireOp",EDGE,"E187.trimOffspring"),sQuery(id+"F3.wireOp",EDGE,"E188.trimOffspring")])],"isStart":false})]});
            var Q8;
            Q8=makeQuery(id+"F1.opExtrude","CAP_EDGE",EDGE,{"disambiguationData":[OSD([sQuery(id+"F0.wireOp",EDGE,"E154.trimOffspring")])],"isStart":true});
            var Q9;
            Q9=makeQuery(id+"F4.boolean.opBoolean","MERGE",EDGE,{"derivedFrom":[makeQuery(id+"F1.opExtrude","CAP_EDGE",EDGE,{"disambiguationData":[OSD([sQuery(id+"F0.wireOp",EDGE,"E24")])],"isStart":true}),makeQuery(id+"F4.opExtrude","CAP_EDGE",EDGE,{"disambiguationData":[OSD([sQuery(id+"F3.wireOp",EDGE,"E166")])],"isStart":false})]});
            var Q10;
            Q10=makeQuery(id+"F4.boolean.opBoolean","MERGE",EDGE,{"derivedFrom":[makeQuery(id+"F1.opExtrude","CAP_EDGE",EDGE,{"disambiguationData":[OSD([sQuery(id+"F0.wireOp",EDGE,"E9.0")])],"isStart":true}),makeQuery(id+"F1.opExtrude","CAP_EDGE",EDGE,{"disambiguationData":[OSD([sQuery(id+"F0.wireOp",EDGE,"E149.trimOffspring")])],"isStart":true}),makeQuery(id+"F4.opExtrude","CAP_EDGE",EDGE,{"disambiguationData":[OSD([sQuery(id+"F3.wireOp",EDGE,"E158.0"),sQuery(id+"F3.wireOp",EDGE,"E193.trimOffspring")])],"isStart":false})]});
            var Q11;
            Q11=makeQuery(id+"F1.opExtrude","CAP_EDGE",EDGE,{"disambiguationData":[OSD([sQuery(id+"F0.wireOp",EDGE,"E8.0")])],"isStart":true});
            var Q12;
            Q12=makeQuery(id+"F4.boolean.opBoolean","MERGE",EDGE,{"derivedFrom":[makeQuery(id+"F1.opExtrude","CAP_EDGE",EDGE,{"disambiguationData":[OSD([sQuery(id+"F0.wireOp",EDGE,"E7.0")])],"isStart":true}),makeQuery(id+"F1.opExtrude","CAP_EDGE",EDGE,{"disambiguationData":[OSD([sQuery(id+"F0.wireOp",EDGE,"E147.trimOffspring")])],"isStart":true}),makeQuery(id+"F1.opExtrude","CAP_EDGE",EDGE,{"disambiguationData":[OSD([sQuery(id+"F0.wireOp",EDGE,"E148.trimOffspring")])],"isStart":true}),makeQuery(id+"F4.opExtrude","CAP_EDGE",EDGE,{"disambiguationData":[OSD([sQuery(id+"F3.wireOp",EDGE,"E156.0"),sQuery(id+"F3.wireOp",EDGE,"E191.trimOffspring"),sQuery(id+"F3.wireOp",EDGE,"E192.trimOffspring")])],"isStart":false})]});
            var Q13;
            Q13=makeQuery(id+"F4.boolean.opBoolean","MERGE",EDGE,{"derivedFrom":[makeQuery(id+"F1.opExtrude","CAP_EDGE",EDGE,{"disambiguationData":[OSD([sQuery(id+"F0.wireOp",EDGE,"E11.trimOffspring")])],"isStart":true}),makeQuery(id+"F1.opExtrude","CAP_EDGE",EDGE,{"disambiguationData":[OSD([sQuery(id+"F0.wireOp",EDGE,"E136.trimOffspring")])],"isStart":true}),makeQuery(id+"F4.opExtrude","CAP_EDGE",EDGE,{"disambiguationData":[OSD([sQuery(id+"F3.wireOp",EDGE,"E159.trimOffspring")])],"isStart":false})]});
            var Q14;
            Q14=makeQuery(id+"F4.boolean.opBoolean","MERGE",EDGE,{"derivedFrom":[makeQuery(id+"F1.opExtrude","CAP_EDGE",EDGE,{"disambiguationData":[OSD([sQuery(id+"F0.wireOp",EDGE,"E1.0")])],"isStart":true}),makeQuery(id+"F1.opExtrude","CAP_EDGE",EDGE,{"disambiguationData":[OSD([sQuery(id+"F0.wireOp",EDGE,"E91.trimOffspring")])],"isStart":true}),makeQuery(id+"F1.opExtrude","CAP_EDGE",EDGE,{"disambiguationData":[OSD([sQuery(id+"F0.wireOp",EDGE,"E92.trimOffspring")])],"isStart":true}),makeQuery(id+"F4.opExtrude","CAP_EDGE",EDGE,{"disambiguationData":[OSD([sQuery(id+"F3.wireOp",EDGE,"E155.0"),sQuery(id+"F3.wireOp",EDGE,"E184.trimOffspring"),sQuery(id+"F3.wireOp",EDGE,"E185.trimOffspring")])],"isStart":false})]});
            var Q15;
            Q15=makeQuery(id+"F4.boolean.opBoolean","MERGE",EDGE,{"derivedFrom":[makeQuery(id+"F1.opExtrude","CAP_EDGE",EDGE,{"disambiguationData":[OSD([sQuery(id+"F0.wireOp",EDGE,"E62.trimOffspring")])],"isStart":true}),makeQuery(id+"F1.opExtrude","CAP_EDGE",EDGE,{"disambiguationData":[OSD([sQuery(id+"F0.wireOp",EDGE,"E150.trimOffspring")])],"isStart":true}),makeQuery(id+"F4.opExtrude","CAP_EDGE",EDGE,{"disambiguationData":[OSD([sQuery(id+"F3.wireOp",EDGE,"E182.trimOffspring"),sQuery(id+"F3.wireOp",EDGE,"E194.trimOffspring")])],"isStart":false})]});
            var Q16;
            Q16=makeQuery(id+"F1.opExtrude","CAP_EDGE",EDGE,{"disambiguationData":[OSD([sQuery(id+"F0.wireOp",EDGE,"E20.0")])],"isStart":true});
            var Q17;
            Q17=makeQuery(id+"F1.opExtrude","CAP_EDGE",EDGE,{"disambiguationData":[OSD([sQuery(id+"F0.wireOp",EDGE,"E19.0")])],"isStart":true});
            var Q18;
            Q18=makeQuery(id+"F1.opExtrude","CAP_EDGE",EDGE,{"disambiguationData":[OSD([sQuery(id+"F0.wireOp",EDGE,"E18.0")])],"isStart":true});
            var Q19;
            Q19=makeQuery(id+"F1.opExtrude","CAP_EDGE",EDGE,{"disambiguationData":[OSD([sQuery(id+"F0.wireOp",EDGE,"E110.trimOffspring")])],"isStart":true});
            var Q20;
            Q20=makeQuery(id+"F4.boolean.opBoolean","MERGE",EDGE,{"derivedFrom":[makeQuery(id+"F1.opExtrude","CAP_EDGE",EDGE,{"disambiguationData":[OSD([sQuery(id+"F0.wireOp",EDGE,"E55.trimOffspring")])],"isStart":true}),makeQuery(id+"F4.opExtrude","CAP_EDGE",EDGE,{"disambiguationData":[OSD([sQuery(id+"F3.wireOp",EDGE,"E180.trimOffspring")])],"isStart":false})]});
            var Q21;
            Q21=makeQuery(id+"F1.opExtrude","CAP_EDGE",EDGE,{"disambiguationData":[OSD([sQuery(id+"F0.wireOp",EDGE,"E45.0")])],"isStart":true});
            var Q22;
            Q22=makeQuery(id+"F4.boolean.opBoolean","MERGE",EDGE,{"derivedFrom":[makeQuery(id+"F1.opExtrude","CAP_EDGE",EDGE,{"disambiguationData":[OSD([sQuery(id+"F0.wireOp",EDGE,"E46.0")])],"isStart":true}),makeQuery(id+"F4.opExtrude","CAP_EDGE",EDGE,{"disambiguationData":[OSD([sQuery(id+"F3.wireOp",EDGE,"E174.0")])],"isStart":false})]});
            var Q23;
            Q23=makeQuery(id+"F1.opExtrude","CAP_EDGE",EDGE,{"disambiguationData":[OSD([sQuery(id+"F0.wireOp",EDGE,"E47.0")])],"isStart":true});
            var Q24;
            Q24=makeQuery(id+"F1.opExtrude","CAP_EDGE",EDGE,{"disambiguationData":[OSD([sQuery(id+"F0.wireOp",EDGE,"E48.0")])],"isStart":true});
            var Q25;
            Q25=makeQuery(id+"F1.opExtrude","CAP_EDGE",EDGE,{"disambiguationData":[OSD([sQuery(id+"F0.wireOp",EDGE,"E49.0")])],"isStart":true});
            var Q26;
            Q26=makeQuery(id+"F4.boolean.opBoolean","MERGE",EDGE,{"derivedFrom":[makeQuery(id+"F1.opExtrude","CAP_EDGE",EDGE,{"disambiguationData":[OSD([sQuery(id+"F0.wireOp",EDGE,"E50.0")])],"isStart":true}),makeQuery(id+"F1.opExtrude","CAP_EDGE",EDGE,{"disambiguationData":[OSD([sQuery(id+"F0.wireOp",EDGE,"E142.trimOffspring")])],"isStart":true}),makeQuery(id+"F4.opExtrude","CAP_EDGE",EDGE,{"disambiguationData":[OSD([sQuery(id+"F3.wireOp",EDGE,"E178.0"),sQuery(id+"F3.wireOp",EDGE,"E190.trimOffspring")])],"isStart":false})]});
            var Q27;
            Q27=makeQuery(id+"F4.boolean.opBoolean","MERGE",EDGE,{"derivedFrom":[makeQuery(id+"F1.opExtrude","CAP_EDGE",EDGE,{"disambiguationData":[OSD([sQuery(id+"F0.wireOp",EDGE,"E51.0")])],"isStart":true}),makeQuery(id+"F4.opExtrude","CAP_EDGE",EDGE,{"disambiguationData":[OSD([sQuery(id+"F3.wireOp",EDGE,"E179.0")])],"isStart":false})]});
            chamfer(context, id + "F8", {"entities" : qUnion([Q0, Q1, Q2, Q3, Q4, Q5, Q6, Q7, Q8, Q9, Q10, Q11, Q12, Q13, Q14, Q15, Q16, Q17, Q18, Q19, Q20, Q21, Q22, Q23, Q24, Q25, Q26, Q27]), "width" : .5 * mm, "tangentPropagation" : true});
        }
    });
